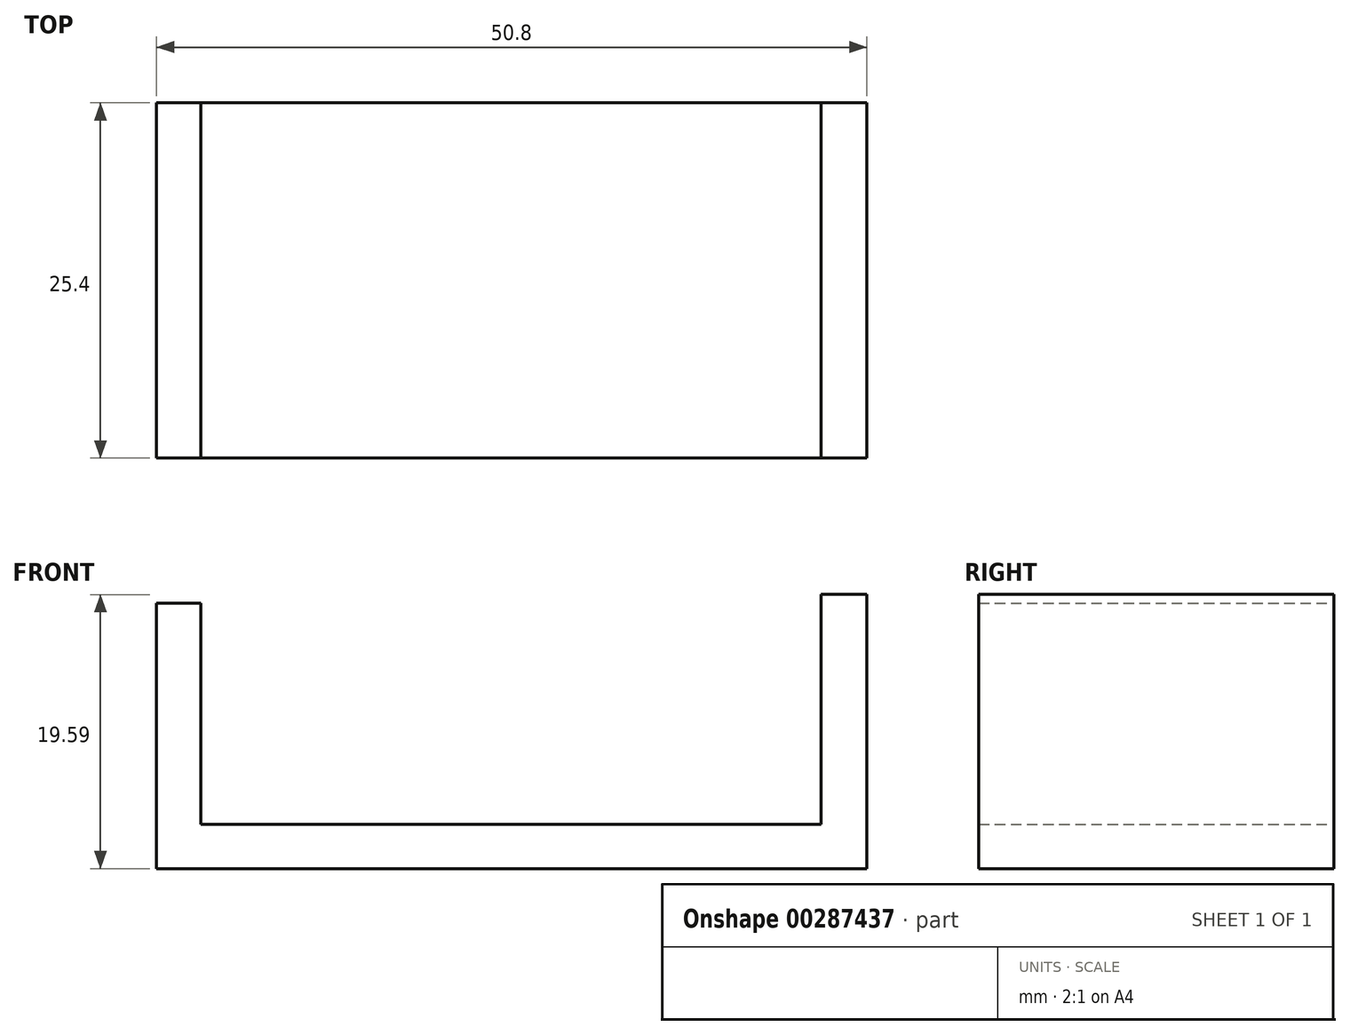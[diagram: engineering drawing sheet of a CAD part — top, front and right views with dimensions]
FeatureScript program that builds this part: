
annotation { "Feature Type Name" : "Feature", "Feature Type Description" : "" }
export const myFeature = defineFeature(function(context is Context, id is Id, definition is map)
    precondition{}
    {
        {
            var Q0;
            Q0=qCreatedBy(makeId("Front.planeOp"),FACE);
            var sketch = newSketch(context, id + "F0", { "sketchPlane" : qUnion([Q0])});
            skLineSegment(sketch, "E0.bottom", {"start": v(13, 0) * mm, "end": v(-37.8, 0) * mm});
            skLineSegment(sketch, "E0.top", {"start": v(13, 3.16) * mm, "end": v(-37.8, 3.16) * mm});
            skLineSegment(sketch, "E0.left", {"start": v(13, 0) * mm, "end": v(13, 3.16) * mm});
            skLineSegment(sketch, "E0.right", {"start": v(-37.8, 0) * mm, "end": v(-37.8, 3.16) * mm});
            skPoint(sketch, "E0.middle", {"position": v(-12.4, 1.58) * mm});
            skLineSegment(sketch, "E1.bottom", {"start": v(-34.63, 18.97) * mm, "end": v(-37.8, 18.97) * mm});
            skLineSegment(sketch, "E1.top", {"start": v(-34.63, 0) * mm, "end": v(-37.8, 0) * mm});
            skLineSegment(sketch, "E1.left", {"start": v(-34.63, 18.97) * mm, "end": v(-34.63, 0) * mm});
            skLineSegment(sketch, "E1.right", {"start": v(-37.8, 18.97) * mm, "end": v(-37.8, 0) * mm});
            skPoint(sketch, "E1.middle", {"position": v(-36.21, 9.48) * mm});
            skLineSegment(sketch, "E2.bottom", {"start": v(9.74, 19.6) * mm, "end": v(13, 19.6) * mm});
            skLineSegment(sketch, "E2.top", {"start": v(9.74, 0) * mm, "end": v(13, 0) * mm});
            skLineSegment(sketch, "E2.left", {"start": v(13, 19.6) * mm, "end": v(13, 0) * mm});
            skLineSegment(sketch, "E2.right", {"start": v(9.74, 19.6) * mm, "end": v(9.74, 0) * mm});
            skSolve(sketch);
        }
        {
            var Q0;
            Q0 = qSketchRegion(id + "F0", true);
            extrude(context, id + "F1", {"entities" : qUnion([Q0]), "endBound" : BoundingType.SYMMETRIC, "depth" : 25.4 * mm});
        }
    });
